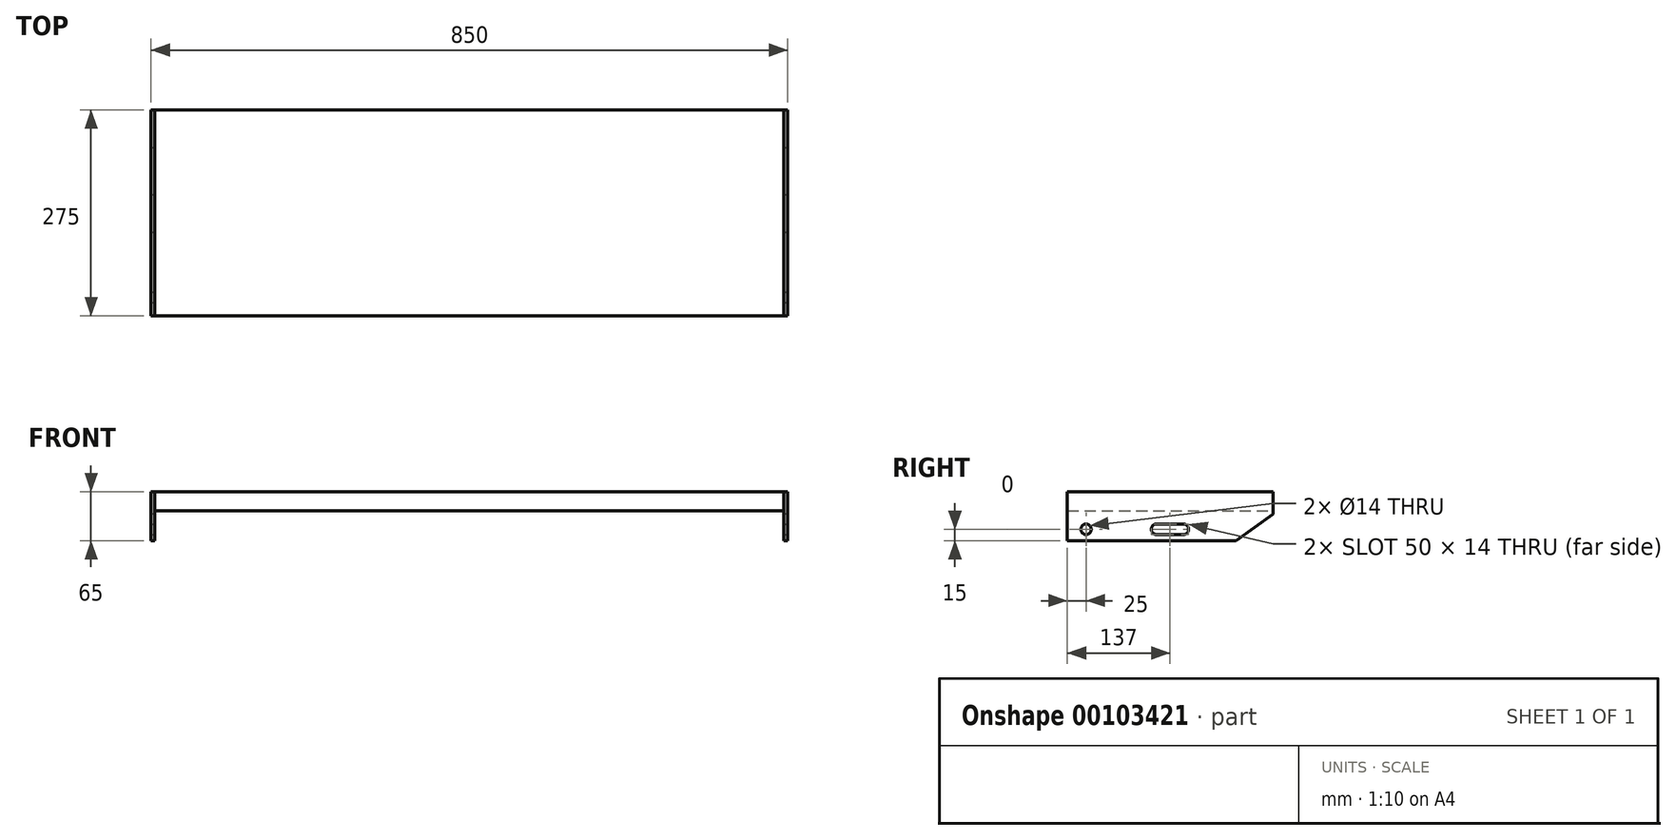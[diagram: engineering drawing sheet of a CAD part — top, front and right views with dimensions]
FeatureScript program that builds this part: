
annotation { "Feature Type Name" : "Feature", "Feature Type Description" : "" }
export const myFeature = defineFeature(function(context is Context, id is Id, definition is map)
    precondition{}
    {
        {
            var Q0;
            Q0=qCreatedBy(makeId("Top.planeOp"),FACE);
            var sketch = newSketch(context, id + "F0", { "sketchPlane" : qUnion([Q0])});
            skLineSegment(sketch, "E0.bottom", {"start": v(-420, 0) * mm, "end": v(420, 0) * mm});
            skLineSegment(sketch, "E0.top", {"start": v(-420, 275) * mm, "end": v(420, 275) * mm});
            skLineSegment(sketch, "E0.left", {"start": v(-420, 0) * mm, "end": v(-420, 275) * mm});
            skLineSegment(sketch, "E0.right", {"start": v(420, 0) * mm, "end": v(420, 275) * mm});
            skSolve(sketch);
        }
        {
            var Q0;
            Q0 = qSketchRegion(id + "F0", true);
            extrude(context, id + "F1", {"entities" : qUnion([Q0]), "oppositeDirection" : true, "depth" : 25 * mm, "offsetDistance" : 25 * mm});
        }
        {
            var Q0;
            Q0=makeQuery(id+"F1.opExtrude","SWEPT_FACE",FACE,{"disambiguationData":[OSD([sQuery(id+"F0.wireOp",EDGE,"E0.right")])]});
            var sketch = newSketch(context, id + "F2", { "sketchPlane" : qUnion([Q0])});
            skLineSegment(sketch, "E1.bottom", {"start": v(0, 0) * mm, "end": v(275, 0) * mm});
            skLineSegment(sketch, "E1.top", {"start": v(0, -65) * mm, "end": v(275, -65) * mm});
            skLineSegment(sketch, "E1.left", {"start": v(0, 0) * mm, "end": v(0, -65) * mm});
            skLineSegment(sketch, "E1.right", {"start": v(275, 0) * mm, "end": v(275, -65) * mm});
            skSolve(sketch);
        }
        {
            var Q0;
            Q0 = qSketchRegion(id + "F2", true);
            extrude(context, id + "F3", {"entities" : qUnion([Q0]), "depth" : 5 * mm, "offsetDistance" : 25 * mm});
        }
        {
            var Q0;
            Q0=makeQuery(id+"F3.opExtrude","SWEPT_EDGE",EDGE,{"disambiguationData":[OSD([sQuery(id+"F2.wireOp",EDGE,"E1.top"),sQuery(id+"F2.wireOp",EDGE,"E1.right")])]});
            chamfer(context, id + "F4", {"entities" : qUnion([Q0]), "chamferType" : ChamferType.OFFSET_ANGLE, "width" : 50 * mm, "oppositeDirection" : true, "angle" : 35 * degree, "tangentPropagation" : true});
        }
        {
            var Q0;
            Q0=makeQuery(id+"F3.opExtrude","CAP_FACE",FACE,{"disambiguationData":[OSD([sQuery(id+"F2.wireOp",EDGE,"E1.bottom"),sQuery(id+"F2.wireOp",EDGE,"E1.top"),sQuery(id+"F2.wireOp",EDGE,"E1.left"),sQuery(id+"F2.wireOp",EDGE,"E1.right")])],"isStart":false});
            var sketch = newSketch(context, id + "F5", { "sketchPlane" : qUnion([Q0])});
            skCircle(sketch, "E2", {"center": v(25, -50) * mm, "radius": 7 * mm});
            skArc(sketch, "E3", {"start": v(119, -43) * mm, "mid": v(112, -50) * mm, "end": v(119, -57) * mm});
            skArc(sketch, "E4", {"start": v(155, -57) * mm, "mid": v(162, -50) * mm, "end": v(155, -43) * mm});
            skLineSegment(sketch, "E5", {"start": v(119, -43) * mm, "end": v(155, -43) * mm});
            skLineSegment(sketch, "E6", {"start": v(119, -57) * mm, "end": v(155, -57) * mm});
            skPoint(sketch, "E7", {"position": v(137, -57) * mm});
            skSolve(sketch);
        }
        {
            var Q0;
            Q0 = qSketchRegion(id + "F5", true);
            extrude(context, id + "F6", {"entities" : qUnion([Q0]), "operationType" : NewBodyOperationType.REMOVE, "oppositeDirection" : true, "depth" : 25 * mm, "offsetDistance" : 25 * mm});
        }
        {
            var Q0;
            Q0=makeQuery(id+"F3.opExtrude","SWEPT_BODY",BODY,{"disambiguationData":[OSD([sQuery(id+"F2.wireOp",EDGE,"E1.bottom"),sQuery(id+"F2.wireOp",EDGE,"E1.top"),sQuery(id+"F2.wireOp",EDGE,"E1.left"),sQuery(id+"F2.wireOp",EDGE,"E1.right")])]});
            var Q1;
            Q1=makeQuery(id+"F3.opExtrude","CAP_VERTEX",VERTEX,{"disambiguationData":[OSD([sQuery(id+"F2.wireOp",EDGE,"E1.bottom"),sQuery(id+"F2.wireOp",EDGE,"E1.left")])],"isStart":false});
            var Q2;
            Q2=makeQuery(id+"F1.opExtrude","CAP_VERTEX",VERTEX,{"disambiguationData":[OSD([sQuery(id+"F0.wireOp",EDGE,"E0.bottom"),sQuery(id+"F0.wireOp",EDGE,"E0.left")])],"isStart":true});
            transform(context, id + "F7", {"entities" : qUnion([Q0]), "transformType" : TransformType.TRANSLATION_ENTITY, "oppositeDirectionEntity" : false, "transformLine" : qUnion([Q1, Q2]), "makeCopy" : true});
        }
        {
            var Q0;
            Q0=makeQuery(id+"F1.opExtrude","SWEPT_BODY",BODY,{"disambiguationData":[OSD([sQuery(id+"F0.wireOp",EDGE,"E0.bottom"),sQuery(id+"F0.wireOp",EDGE,"E0.top"),sQuery(id+"F0.wireOp",EDGE,"E0.left"),sQuery(id+"F0.wireOp",EDGE,"E0.right")])]});
            transform(context, id + "F8", {"entities" : qUnion([Q0]), "transformType" : TransformType.TRANSLATION_3D, "dx" : 0 * mm, "dy" : 0 * mm, "dz" : 0 * mm, "makeCopy" : true});
        }
        {
            var Q0;
            Q0=makeQuery(id+"F1.opExtrude","SWEPT_BODY",BODY,{"disambiguationData":[OSD([sQuery(id+"F0.wireOp",EDGE,"E0.bottom"),sQuery(id+"F0.wireOp",EDGE,"E0.top"),sQuery(id+"F0.wireOp",EDGE,"E0.left"),sQuery(id+"F0.wireOp",EDGE,"E0.right")])]});
            deleteBodies(context, id + "F9", {"entities" : qUnion([Q0])});
        }
    });
